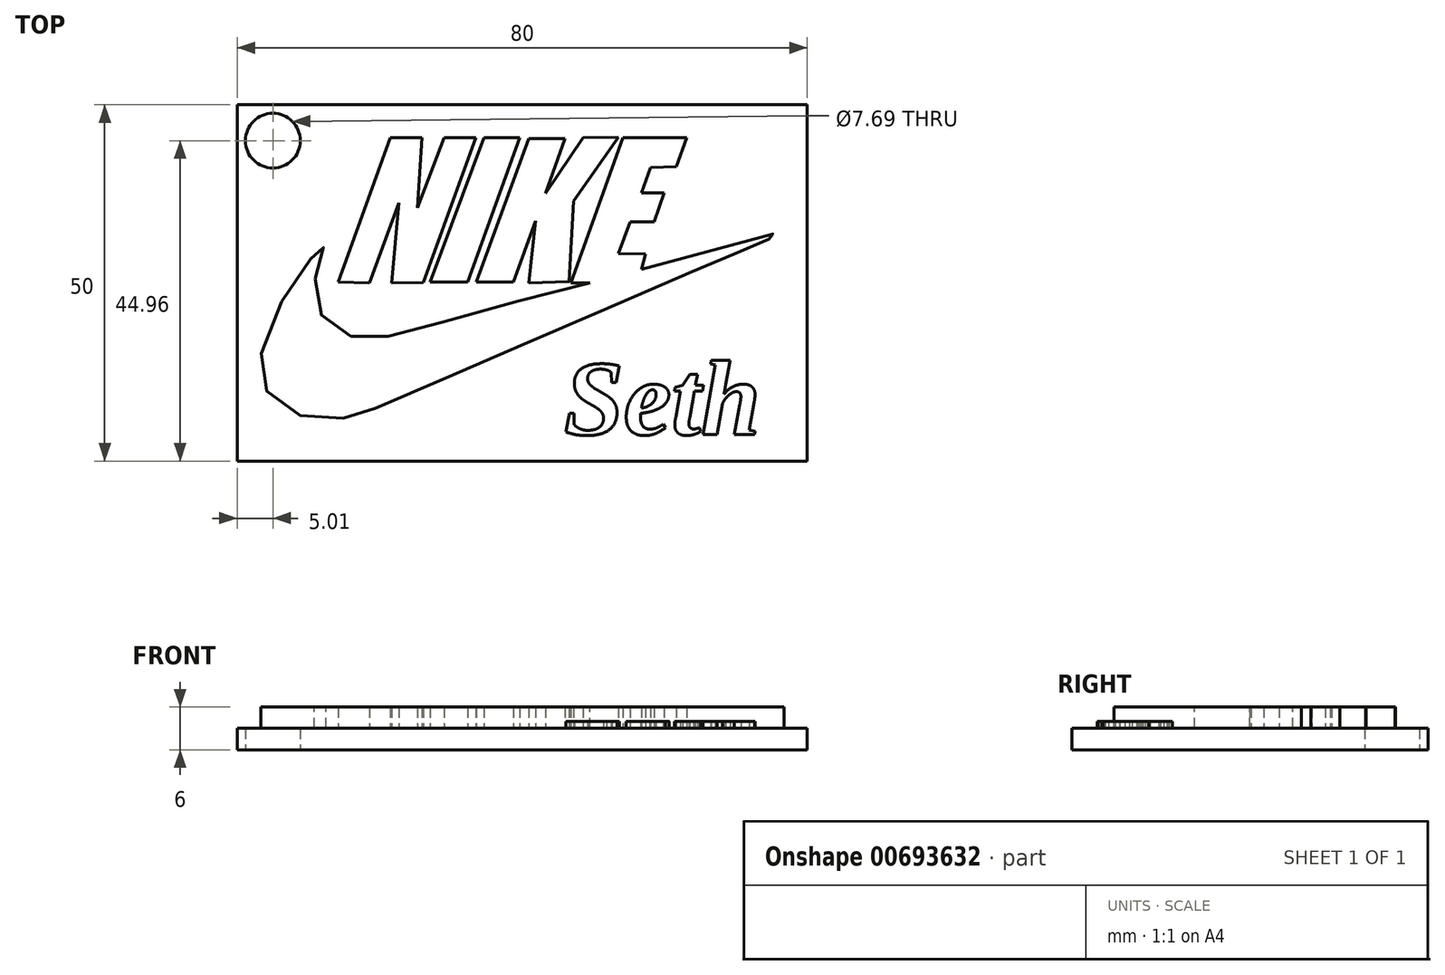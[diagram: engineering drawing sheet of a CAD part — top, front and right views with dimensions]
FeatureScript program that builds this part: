
annotation { "Feature Type Name" : "Feature", "Feature Type Description" : "" }
export const myFeature = defineFeature(function(context is Context, id is Id, definition is map)
    precondition{}
    {
        {
            var Q0;
            Q0=qCreatedBy(makeId("Top.planeOp"),FACE);
            var sketch = newSketch(context, id + "F0", { "sketchPlane" : qUnion([Q0])});
            skLineSegment(sketch, "E0", {"start": v(-40, 26.78) * mm, "end": v(40, 26.78) * mm});
            skLineSegment(sketch, "E1", {"start": v(40, 26.78) * mm, "end": v(40, -23.22) * mm});
            skLineSegment(sketch, "E2", {"start": v(40, -23.22) * mm, "end": v(-40, -23.22) * mm});
            skLineSegment(sketch, "E3", {"start": v(-40, -23.22) * mm, "end": v(-40, 26.78) * mm});
            skCircle(sketch, "E4", {"center": v(-34.99, 21.74) * mm, "radius": 3.85 * mm});
            skSolve(sketch);
        }
        {
            var Q0;
            Q0=makeQuery(id+"F0.imprint","IMPRINT",FACE,{"disambiguationData":[TD([[makeQuery(id+"F0.imprint","IMPRINT",EDGE,{"derivedFrom":sQuery(id+"F0.wireOp",EDGE,"E0")}),-1.0]])]});
            extrude(context, id + "F1", {"entities" : qUnion([Q0]), "depth" : 3 * mm, "offsetDistance" : 25 * mm});
        }
        {
            var Q0;
            Q0=qCreatedBy(makeId("Top.planeOp"),FACE);
            var sketch = newSketch(context, id + "F2", { "sketchPlane" : qUnion([Q0])});
            skFitSpline(sketch, "E5", {"points": [v(36.75, 8.98) * mm, v(35.1, 8.16) * mm, v(33.87, 7.6) * mm, v(32.51, 7.03) * mm, v(30.26, 6.06) * mm, v(26.9, 4.66) * mm, v(25.94, 4.26) * mm, v(22.55, 2.78) * mm, v(20.52, 1.89) * mm, v(17.53, 0.6) * mm, v(16.75, 0.28) * mm, v(11.98, -1.78) * mm, v(8.66, -3.18) * mm, v(-4.23, -8.75) * mm, v(-11.08, -11.7) * mm, v(-18.92, -15.1) * mm, v(-22.32, -16.53) * mm, v(-23.4, -16.89) * mm, v(-24.37, -17.11) * mm, v(-25.8, -17.27) * mm, v(-28.49, -17.27) * mm, v(-31.03, -16.87) * mm, v(-33.04, -15.9) * mm, v(-34.98, -14.52) * mm, v(-36.21, -12.66) * mm, v(-36.63, -11) * mm, v(-36.63, -8.72) * mm, v(-36.28, -6.64) * mm, v(-34.23, -1.71) * mm, v(-32.88, 0.58) * mm, v(-31.67, 2.42) * mm, v(-27.95, 7.36) * mm, v(-27.5, 7.8) * mm, v(-27.57, 7.64) * mm, v(-27.68, 7.38) * mm, v(-27.81, 7.01) * mm, v(-28.22, 5.65) * mm, v(-28.66, 4.27) * mm, v(-28.88, 3.32) * mm, v(-29.12, 1.54) * mm, v(-29.04, -0.66) * mm, v(-28.49, -2.24) * mm, v(-27.67, -3.44) * mm, v(-25.91, -5) * mm, v(-24.45, -5.59) * mm, v(-23.32, -5.9) * mm, v(-22.36, -5.99) * mm, v(-19.8, -5.91) * mm, v(-16.75, -5.16) * mm, v(-13.07, -4.22) * mm, v(-4.74, -1.94) * mm, v(1.36, -0.28) * mm, v(7.68, 1.3) * mm, v(34.67, 8.52) * mm, v(35.9, 8.83) * mm, v(36.48, 8.95) * mm, v(36.75, 8.98) * mm]});
            skLineSegment(sketch, "E6", {"start": v(-25.82, 1.88) * mm, "end": v(-18.51, 22.14) * mm});
            skLineSegment(sketch, "E7", {"start": v(-18.51, 22.14) * mm, "end": v(-14.08, 22.14) * mm});
            skLineSegment(sketch, "E8", {"start": v(-14.08, 22.14) * mm, "end": v(-14.69, 12.35) * mm});
            skLineSegment(sketch, "E9", {"start": v(-14.69, 12.35) * mm, "end": v(-10.96, 22.2) * mm});
            skLineSegment(sketch, "E10", {"start": v(-10.96, 22.2) * mm, "end": v(-6.52, 22.2) * mm});
            skLineSegment(sketch, "E11", {"start": v(-6.52, 22.2) * mm, "end": v(-13.87, 1.82) * mm});
            skLineSegment(sketch, "E12", {"start": v(-13.87, 1.82) * mm, "end": v(-18.32, 1.75) * mm});
            skLineSegment(sketch, "E13", {"start": v(-18.32, 1.75) * mm, "end": v(-17.32, 13.05) * mm});
            skLineSegment(sketch, "E14", {"start": v(-17.32, 13.05) * mm, "end": v(-21.43, 1.75) * mm});
            skLineSegment(sketch, "E15", {"start": v(-21.43, 1.75) * mm, "end": v(-25.82, 1.88) * mm});
            skLineSegment(sketch, "E16", {"start": v(-12.9, 1.88) * mm, "end": v(-5.4, 22.17) * mm});
            skLineSegment(sketch, "E17", {"start": v(-5.4, 22.17) * mm, "end": v(-0.34, 22.17) * mm});
            skLineSegment(sketch, "E18", {"start": v(-0.34, 22.17) * mm, "end": v(-7.63, 1.88) * mm});
            skLineSegment(sketch, "E19", {"start": v(-7.63, 1.88) * mm, "end": v(-12.9, 1.88) * mm});
            skLineSegment(sketch, "E20", {"start": v(-6.42, 1.88) * mm, "end": v(0.9, 22.05) * mm});
            skLineSegment(sketch, "E21", {"start": v(0.9, 22.05) * mm, "end": v(6, 22.05) * mm});
            skLineSegment(sketch, "E22", {"start": v(6, 22.05) * mm, "end": v(3.28, 14.38) * mm});
            skLineSegment(sketch, "E23", {"start": v(3.28, 14.38) * mm, "end": v(8.53, 22.16) * mm});
            skLineSegment(sketch, "E24", {"start": v(8.53, 22.16) * mm, "end": v(13.51, 22.2) * mm});
            skLineSegment(sketch, "E25", {"start": v(13.51, 22.2) * mm, "end": v(7.2, 13.25) * mm});
            skLineSegment(sketch, "E26", {"start": v(7.2, 13.25) * mm, "end": v(6.57, 1.96) * mm});
            skLineSegment(sketch, "E27", {"start": v(6.57, 1.96) * mm, "end": v(0.9, 1.81) * mm});
            skLineSegment(sketch, "E28", {"start": v(0.9, 1.81) * mm, "end": v(1.89, 10.46) * mm});
            skLineSegment(sketch, "E29", {"start": v(1.89, 10.46) * mm, "end": v(-1.25, 1.88) * mm});
            skLineSegment(sketch, "E30", {"start": v(-1.25, 1.88) * mm, "end": v(-6.42, 1.88) * mm});
            skLineSegment(sketch, "E31", {"start": v(14.12, 22.15) * mm, "end": v(23.05, 22.15) * mm});
            skLineSegment(sketch, "E32", {"start": v(23.05, 22.15) * mm, "end": v(21.64, 18.08) * mm});
            skLineSegment(sketch, "E33", {"start": v(21.64, 18.08) * mm, "end": v(18.02, 17.99) * mm});
            skLineSegment(sketch, "E34", {"start": v(18.02, 17.99) * mm, "end": v(16.7, 14.4) * mm});
            skLineSegment(sketch, "E35", {"start": v(16.7, 14.4) * mm, "end": v(19.93, 14.4) * mm});
            skLineSegment(sketch, "E36", {"start": v(19.93, 14.4) * mm, "end": v(18.5, 10.35) * mm});
            skLineSegment(sketch, "E37", {"start": v(18.5, 10.35) * mm, "end": v(15.14, 10.35) * mm});
            skLineSegment(sketch, "E38", {"start": v(15.14, 10.35) * mm, "end": v(13.5, 5.88) * mm});
            skLineSegment(sketch, "E39", {"start": v(13.5, 5.88) * mm, "end": v(17.33, 5.85) * mm});
            skLineSegment(sketch, "E40", {"start": v(17.33, 5.85) * mm, "end": v(16.71, 3.7) * mm});
            skLineSegment(sketch, "E41", {"start": v(16.71, 3.7) * mm, "end": v(9.5, 1.78) * mm});
            skLineSegment(sketch, "E42", {"start": v(9.5, 1.78) * mm, "end": v(6.8, 1.78) * mm});
            skLineSegment(sketch, "E43", {"start": v(6.8, 1.78) * mm, "end": v(14.12, 22.15) * mm});
            skSolve(sketch);
        }
        {
            var Q0;
            Q0 = qSketchRegion(id + "F2", true);
            extrude(context, id + "F3", {"entities" : qUnion([Q0]), "operationType" : NewBodyOperationType.ADD, "depth" : 6 * mm, "offsetDistance" : 25 * mm});
        }
        {
            var Q0;
            Q0=makeQuery(id+"F1.opExtrude","CAP_FACE",FACE,{"disambiguationData":[OSD([sQuery(id+"F0.wireOp",EDGE,"E0"),sQuery(id+"F0.wireOp",EDGE,"E1"),sQuery(id+"F0.wireOp",EDGE,"E2"),sQuery(id+"F0.wireOp",EDGE,"E3"),sQuery(id+"F0.wireOp",EDGE,"E4")])],"isStart":false});
            var sketch = newSketch(context, id + "F4", { "sketchPlane" : qUnion([Q0])});
            skText(sketch, "E44", { "text": "Seth", "fontName": "Tinos-BoldItalic.ttf"});
            const initialGuessF4  = {"E44": [0.00588, -0.0195, 1, 0, 0.01082]};
            skSetInitialGuess(sketch, initialGuessF4);
            skSolve(sketch);
        }
        {
            var Q0;
            Q0 = qSketchRegion(id + "F4", true);
            extrude(context, id + "F5", {"entities" : qUnion([Q0]), "operationType" : NewBodyOperationType.ADD, "depth" : 1 * mm, "offsetDistance" : 25 * mm});
        }
    });
